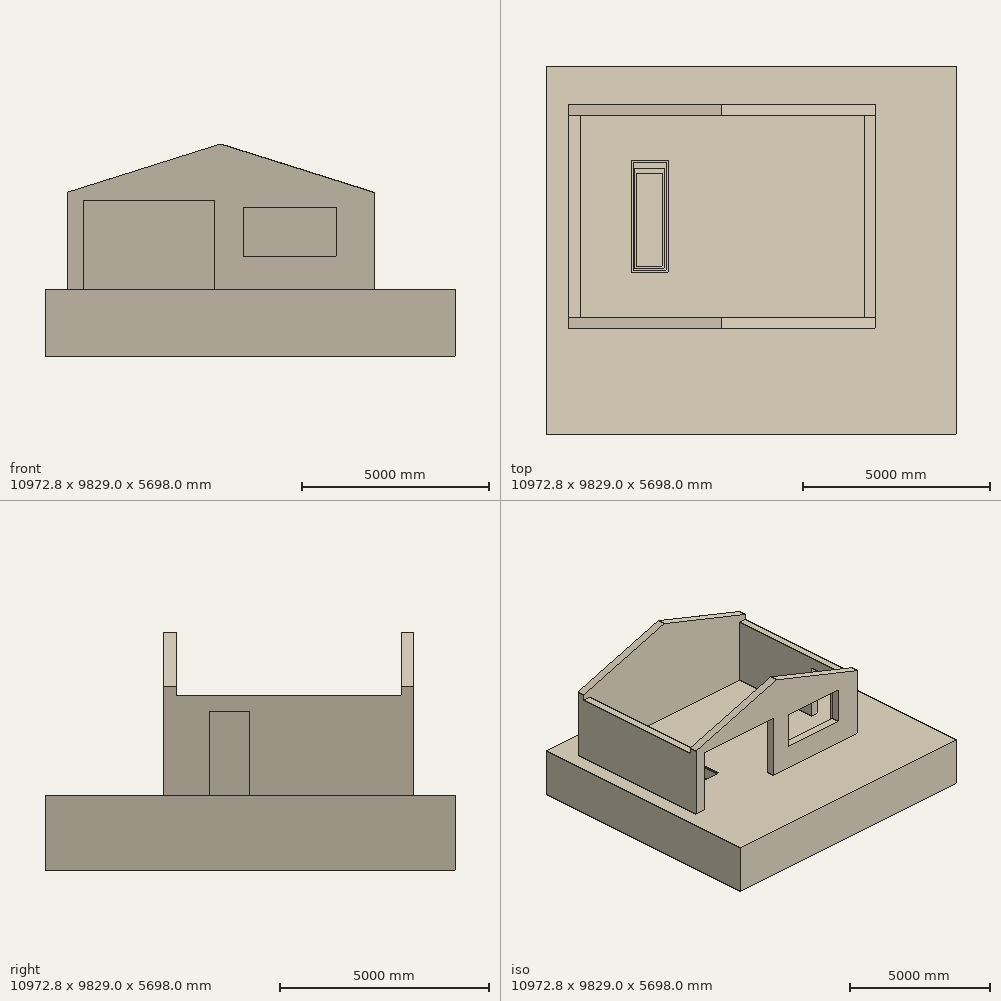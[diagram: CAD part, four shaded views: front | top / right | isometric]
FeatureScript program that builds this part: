
annotation { "Feature Type Name" : "Feature", "Feature Type Description" : "" }
export const myFeature = defineFeature(function(context is Context, id is Id, definition is map)
    precondition{}
    {
        {
            var Q0;
            Q0=qCreatedBy(makeId("Top.planeOp"),FACE);
            var sketch = newSketch(context, id + "F0", { "sketchPlane" : qUnion([Q0])});
            skLineSegment(sketch, "E0.bottom", {"start": v(-4093.64, 2707.76) * mm, "end": v(4106.36, 2707.76) * mm});
            skLineSegment(sketch, "E0.top", {"start": v(-4093.64, -3292.24) * mm, "end": v(4106.36, -3292.24) * mm});
            skLineSegment(sketch, "E0.left", {"start": v(-4093.64, 2707.76) * mm, "end": v(-4093.64, -3292.24) * mm});
            skLineSegment(sketch, "E0.right", {"start": v(4106.36, 2707.76) * mm, "end": v(4106.36, -3292.24) * mm});
            skSolve(sketch);
        }
        {
            var Q0;
            Q0=makeQuery(id+"F0.imprint","IMPRINT",FACE,{"disambiguationData":[TD([[makeQuery(id+"F0.imprint","IMPRINT",EDGE,{"derivedFrom":sQuery(id+"F0.wireOp",EDGE,"E0.bottom")}),-1.0]])]});
            extrude(context, id + "F1", {"entities" : qUnion([Q0]), "depth" : 2400 * mm, "offsetDistance" : 25 * mm});
        }
        {
            var Q0;
            Q0=makeQuery(id+"F1.opExtrude","CAP_FACE",FACE,{"disambiguationData":[OSD([sQuery(id+"F0.wireOp",EDGE,"E0.bottom"),sQuery(id+"F0.wireOp",EDGE,"E0.top"),sQuery(id+"F0.wireOp",EDGE,"E0.left"),sQuery(id+"F0.wireOp",EDGE,"E0.right")])],"isStart":false});
            var sketch = newSketch(context, id + "F2", { "sketchPlane" : qUnion([Q0])});
            skLineSegment(sketch, "E1.bottom", {"start": v(-3793.64, 2407.76) * mm, "end": v(3806.36, 2407.76) * mm});
            skLineSegment(sketch, "E1.top", {"start": v(-3793.64, -2992.24) * mm, "end": v(3806.36, -2992.24) * mm});
            skLineSegment(sketch, "E1.left", {"start": v(-3793.64, 2407.76) * mm, "end": v(-3793.64, -2992.24) * mm});
            skLineSegment(sketch, "E1.right", {"start": v(3806.36, 2407.76) * mm, "end": v(3806.36, -2992.24) * mm});
            skSolve(sketch);
        }
        {
            var Q0;
            Q0 = qSketchRegion(id + "F2", true);
            extrude(context, id + "F3", {"entities" : qUnion([Q0]), "operationType" : NewBodyOperationType.REMOVE, "endBound" : BoundingType.UP_TO_NEXT, "oppositeDirection" : true, "depth" : 25 * mm, "offsetDistance" : 25 * mm});
        }
        {
            var Q0;
            Q0=makeQuery(id+"F1.opExtrude","CAP_FACE",FACE,{"disambiguationData":[OSD([sQuery(id+"F0.wireOp",EDGE,"E0.bottom"),sQuery(id+"F0.wireOp",EDGE,"E0.top"),sQuery(id+"F0.wireOp",EDGE,"E0.left"),sQuery(id+"F0.wireOp",EDGE,"E0.right")])],"isStart":true});
            var sketch = newSketch(context, id + "F4", { "sketchPlane" : qUnion([Q0])});
            skLineSegment(sketch, "E2.bottom", {"start": v(-4693.64, -3707.76) * mm, "end": v(6279.16, -3707.76) * mm});
            skLineSegment(sketch, "E2.top", {"start": v(-4693.64, 6121.2) * mm, "end": v(6279.16, 6121.2) * mm});
            skLineSegment(sketch, "E2.left", {"start": v(-4693.64, -3707.76) * mm, "end": v(-4693.64, 6121.2) * mm});
            skLineSegment(sketch, "E2.right", {"start": v(6279.16, -3707.76) * mm, "end": v(6279.16, 6121.2) * mm});
            skSolve(sketch);
        }
        {
            var Q0;
            Q0 = qSketchRegion(id + "F4", true);
            extrude(context, id + "F5", {"entities" : qUnion([Q0]), "operationType" : NewBodyOperationType.ADD, "depth" : 1800 * mm, "offsetDistance" : 25 * mm});
        }
        {
            var Q0;
            Q0=makeQuery(id+"F1.opExtrude","SWEPT_FACE",FACE,{"disambiguationData":[OSD([sQuery(id+"F0.wireOp",EDGE,"E0.top")])]});
            var sketch = newSketch(context, id + "F6", { "sketchPlane" : qUnion([Q0])});
            skLineSegment(sketch, "E3.bottom", {"start": v(-3678.64, 2375) * mm, "end": v(-178.64, 2375) * mm});
            skLineSegment(sketch, "E3.top", {"start": v(-3678.64, 0) * mm, "end": v(-178.64, 0) * mm});
            skLineSegment(sketch, "E3.left", {"start": v(-3678.64, 2375) * mm, "end": v(-3678.64, 0) * mm});
            skLineSegment(sketch, "E3.right", {"start": v(-178.64, 2375) * mm, "end": v(-178.64, 0) * mm});
            skSolve(sketch);
        }
        {
            var Q0;
            Q0 = qSketchRegion(id + "F6", true);
            extrude(context, id + "F7", {"entities" : qUnion([Q0]), "operationType" : NewBodyOperationType.REMOVE, "endBound" : BoundingType.UP_TO_NEXT, "oppositeDirection" : true, "depth" : 25 * mm, "offsetDistance" : 25 * mm});
        }
        {
            var Q0;
            Q0=makeQuery(id+"F1.opExtrude","SWEPT_FACE",FACE,{"disambiguationData":[OSD([sQuery(id+"F0.wireOp",EDGE,"E0.top")])]});
            var sketch = newSketch(context, id + "F8", { "sketchPlane" : qUnion([Q0])});
            skLineSegment(sketch, "E4.bottom", {"start": v(606.36, 2208.56) * mm, "end": v(3106.36, 2208.56) * mm});
            skLineSegment(sketch, "E4.top", {"start": v(606.36, 900) * mm, "end": v(3106.36, 900) * mm});
            skLineSegment(sketch, "E4.left", {"start": v(606.36, 2208.56) * mm, "end": v(606.36, 900) * mm});
            skLineSegment(sketch, "E4.right", {"start": v(3106.36, 2208.56) * mm, "end": v(3106.36, 900) * mm});
            skSolve(sketch);
        }
        {
            var Q0;
            {var subQ10=sQuery(id+"F8.wireOp",EDGE,"E4.top");Q0=makeQuery(id+"F8.imprint","IMPRINT",FACE,{"disambiguationData":[TD([[makeQuery(id+"F8.imprint","IMPRINT",EDGE,{"derivedFrom":subQ10}),-1.0]])]});}
            var sketch = newSketch(context, id + "F9", { "sketchPlane" : qUnion([Q0])});
            skLineSegment(sketch, "E5", {"start": v(-4093.64, 2607.28) * mm, "end": v(0, 3898) * mm});
            skLineSegment(sketch, "E6", {"start": v(0, 3898) * mm, "end": v(4106.36, 2603.27) * mm});
            skLineSegment(sketch, "E7", {"start": v(-4093.64, 2400) * mm, "end": v(-4093.64, 2607.28) * mm});
            skLineSegment(sketch, "E8", {"start": v(4106.36, 2400) * mm, "end": v(4106.36, 2603.27) * mm});
            skLineSegment(sketch, "E9", {"start": v(-4093.64, 2400) * mm, "end": v(4106.36, 2400) * mm});
            skSolve(sketch);
        }
        {
            var Q0;
            Q0 = qSketchRegion(id + "F9", true);
            extrude(context, id + "F10", {"entities" : qUnion([Q0]), "operationType" : NewBodyOperationType.ADD, "oppositeDirection" : true, "depth" : 300 * mm, "offsetDistance" : 25 * mm});
        }
        {
            var Q0;
            Q0 = qSketchRegion(id + "F8", true);
            extrude(context, id + "F11", {"entities" : qUnion([Q0]), "operationType" : NewBodyOperationType.REMOVE, "endBound" : BoundingType.UP_TO_NEXT, "oppositeDirection" : true, "depth" : 25 * mm, "offsetDistance" : 25 * mm});
        }
        {
            var Q0;
            Q0=makeQuery(id+"F3.boolean.opBoolean","COPY",FACE,{"derivedFrom":makeQuery(id+"F3.opExtrude","SWEPT_FACE",FACE,{"disambiguationData":[OSD([sQuery(id+"F2.wireOp",EDGE,"E1.right")])]})});
            var sketch = newSketch(context, id + "F12", { "sketchPlane" : qUnion([Q0])});
            skLineSegment(sketch, "E10.bottom", {"start": v(1242.24, 2000) * mm, "end": v(2192.24, 2000) * mm});
            skLineSegment(sketch, "E10.top", {"start": v(1242.24, 0) * mm, "end": v(2192.24, 0) * mm});
            skLineSegment(sketch, "E10.left", {"start": v(1242.24, 2000) * mm, "end": v(1242.24, 0) * mm});
            skLineSegment(sketch, "E10.right", {"start": v(2192.24, 2000) * mm, "end": v(2192.24, 0) * mm});
            skSolve(sketch);
        }
        {
            var Q0;
            Q0 = qSketchRegion(id + "F12", true);
            extrude(context, id + "F13", {"entities" : qUnion([Q0]), "operationType" : NewBodyOperationType.REMOVE, "endBound" : BoundingType.UP_TO_NEXT, "oppositeDirection" : true, "depth" : 25 * mm, "offsetDistance" : 25 * mm});
        }
        {
            var Q0;
            Q0=makeQuery(id+"F1.opExtrude","SWEPT_FACE",FACE,{"disambiguationData":[OSD([sQuery(id+"F0.wireOp",EDGE,"E0.bottom")])]});
            var sketch = newSketch(context, id + "F14", { "sketchPlane" : qUnion([Q0])});
            skLineSegment(sketch, "E11", {"start": v(-4106.36, 2400) * mm, "end": v(-4106.36, 2603.27) * mm});
            skLineSegment(sketch, "E12", {"start": v(-4106.36, 2603.27) * mm, "end": v(0, 3898) * mm});
            skLineSegment(sketch, "E13", {"start": v(0, 3898) * mm, "end": v(4093.64, 2607.28) * mm});
            skLineSegment(sketch, "E14", {"start": v(4093.64, 2607.28) * mm, "end": v(4093.64, 2400) * mm});
            skLineSegment(sketch, "E15", {"start": v(-4106.36, 2400) * mm, "end": v(4093.64, 2400) * mm});
            skSolve(sketch);
        }
        {
            var Q0;
            Q0 = qSketchRegion(id + "F14", true);
            extrude(context, id + "F15", {"entities" : qUnion([Q0]), "operationType" : NewBodyOperationType.ADD, "oppositeDirection" : true, "depth" : 300 * mm, "offsetDistance" : 25 * mm});
        }
        {
            var Q0;
            {var subQ0=sQuery(id+"F4.wireOp",EDGE,"E2.right");var subQ1=sQuery(id+"F4.wireOp",EDGE,"E2.left");var subQ2=sQuery(id+"F4.wireOp",EDGE,"E2.top");var subQ3=sQuery(id+"F4.wireOp",EDGE,"E2.bottom");var subQ4=makeQuery(id+"F5.opExtrude","CAP_FACE",FACE,{"disambiguationData":[OSD([subQ3,subQ2,subQ1,subQ0])],"isStart":true});Q0=makeQuery(id+"F13.boolean.opBoolean","MERGE",FACE,{"derivedFrom":[makeQuery(id+"F7.boolean.opBoolean","MERGE",FACE,{"derivedFrom":[makeQuery(id+"F5.boolean.opBoolean","SPLIT",FACE,{"disambiguationData":[TD([makeQuery(id+"F1.opExtrude","SWEPT_FACE",FACE,{"disambiguationData":[OSD([sQuery(id+"F0.wireOp",EDGE,"E0.bottom")])]})])],"derivedFrom":subQ4}),makeQuery(id+"F5.boolean.opBoolean","SPLIT",FACE,{"disambiguationData":[TD([makeQuery(id+"F3.boolean.opBoolean","COPY",FACE,{"derivedFrom":makeQuery(id+"F3.opExtrude","SWEPT_FACE",FACE,{"disambiguationData":[OSD([sQuery(id+"F2.wireOp",EDGE,"E1.bottom")])]})})])],"derivedFrom":subQ4}),makeQuery(id+"F7.opExtrude","SWEPT_FACE",FACE,{"disambiguationData":[OSD([sQuery(id+"F6.wireOp",EDGE,"E3.top")])]})]}),makeQuery(id+"F13.opExtrude","SWEPT_FACE",FACE,{"disambiguationData":[OSD([sQuery(id+"F12.wireOp",EDGE,"E10.top")])]})]});}
            var sketch = newSketch(context, id + "F16", { "sketchPlane" : qUnion([Q0])});
            skLineSegment(sketch, "E16.bottom", {"start": v(-2428.64, 1207.76) * mm, "end": v(-1428.64, 1207.76) * mm});
            skLineSegment(sketch, "E16.top", {"start": v(-2428.64, -1792.24) * mm, "end": v(-1428.64, -1792.24) * mm});
            skLineSegment(sketch, "E16.left", {"start": v(-2428.64, 1207.76) * mm, "end": v(-2428.64, -1792.24) * mm});
            skLineSegment(sketch, "E16.right", {"start": v(-1428.64, 1207.76) * mm, "end": v(-1428.64, -1792.24) * mm});
            skLineSegment(sketch, "E17", {"start": v(-3678.64, -3292.24) * mm, "end": v(-178.64, -3292.24) * mm});
            skLineSegment(sketch, "E18", {"start": v(-178.64, -3292.24) * mm, "end": v(-1928.64, -3292.24) * mm});
            skLineSegment(sketch, "E19", {"start": v(-1928.64, 1207.76) * mm, "end": v(-1928.64, -1792.24) * mm, "construction": true});
            skLineSegment(sketch, "E20", {"start": v(-1928.64, -3292.24) * mm, "end": v(-1928.64, 2407.76) * mm, "construction": true});
            skPoint(sketch, "E21.startSnap0", {"position": v(-1928.64, -442.24) * mm});
            skLineSegment(sketch, "E22", {"start": v(-3793.64, -292.24) * mm, "end": v(1314.81, -292.24) * mm, "construction": true});
            skLineSegment(sketch, "E23", {"start": v(-2428.64, -292.24) * mm, "end": v(-1428.64, -292.24) * mm, "construction": true});
            skSolve(sketch);
        }
        {
            var Q0;
            Q0 = qSketchRegion(id + "F16", true);
            extrude(context, id + "F17", {"entities" : qUnion([Q0]), "operationType" : NewBodyOperationType.REMOVE, "oppositeDirection" : true, "depth" : 30 * mm, "offsetDistance" : 25 * mm});
        }
        {
            var Q0;
            Q0=makeQuery(id+"F17.boolean.opBoolean","COPY",FACE,{"derivedFrom":makeQuery(id+"F17.opExtrude","CAP_FACE",FACE,{"disambiguationData":[OSD([sQuery(id+"F16.wireOp",EDGE,"E16.bottom"),sQuery(id+"F16.wireOp",EDGE,"E16.top"),sQuery(id+"F16.wireOp",EDGE,"E16.left"),sQuery(id+"F16.wireOp",EDGE,"E16.right")])],"isStart":false})});
            var sketch = newSketch(context, id + "F18", { "sketchPlane" : qUnion([Q0])});
            skLineSegment(sketch, "E24.bottom", {"start": v(-2378.64, 1157.76) * mm, "end": v(-1478.64, 1157.76) * mm});
            skLineSegment(sketch, "E24.top", {"start": v(-2378.64, -1742.24) * mm, "end": v(-1478.64, -1742.24) * mm});
            skLineSegment(sketch, "E24.left", {"start": v(-2378.64, 1157.76) * mm, "end": v(-2378.64, -1742.24) * mm});
            skLineSegment(sketch, "E24.right", {"start": v(-1478.64, 1157.76) * mm, "end": v(-1478.64, -1742.24) * mm});
            skSolve(sketch);
        }
        {
            var Q0;
            Q0 = qSketchRegion(id + "F18", true);
            extrude(context, id + "F19", {"entities" : qUnion([Q0]), "operationType" : NewBodyOperationType.REMOVE, "oppositeDirection" : true, "depth" : 423.33 * mm, "offsetDistance" : 25 * mm});
        }
        {
            var Q0;
            Q0=makeQuery(id+"F19.boolean.opBoolean","COPY",FACE,{"derivedFrom":makeQuery(id+"F19.opExtrude","CAP_FACE",FACE,{"disambiguationData":[OSD([sQuery(id+"F18.wireOp",EDGE,"E24.bottom"),sQuery(id+"F18.wireOp",EDGE,"E24.top"),sQuery(id+"F18.wireOp",EDGE,"E24.left"),sQuery(id+"F18.wireOp",EDGE,"E24.right")])],"isStart":false})});
            var sketch = newSketch(context, id + "F20", { "sketchPlane" : qUnion([Q0])});
            skLineSegment(sketch, "E25.bottom", {"start": v(-2328.64, 982.76) * mm, "end": v(-1528.64, 982.76) * mm});
            skLineSegment(sketch, "E25.top", {"start": v(-2328.64, -1692.24) * mm, "end": v(-1528.64, -1692.24) * mm});
            skLineSegment(sketch, "E25.left", {"start": v(-2328.64, 982.76) * mm, "end": v(-2328.64, -1692.24) * mm});
            skLineSegment(sketch, "E25.right", {"start": v(-1528.64, 982.76) * mm, "end": v(-1528.64, -1692.24) * mm});
            skSolve(sketch);
        }
        {
            var Q0;
            Q0 = qSketchRegion(id + "F20", true);
            extrude(context, id + "F21", {"entities" : qUnion([Q0]), "operationType" : NewBodyOperationType.REMOVE, "oppositeDirection" : true, "depth" : 423.33 * mm, "offsetDistance" : 25 * mm});
        }
        {
            var Q0;
            Q0=makeQuery(id+"F21.boolean.opBoolean","COPY",FACE,{"derivedFrom":makeQuery(id+"F21.opExtrude","CAP_FACE",FACE,{"disambiguationData":[OSD([sQuery(id+"F20.wireOp",EDGE,"E25.bottom"),sQuery(id+"F20.wireOp",EDGE,"E25.top"),sQuery(id+"F20.wireOp",EDGE,"E25.left"),sQuery(id+"F20.wireOp",EDGE,"E25.right")])],"isStart":false})});
            var sketch = newSketch(context, id + "F22", { "sketchPlane" : qUnion([Q0])});
            skLineSegment(sketch, "E26.bottom", {"start": v(-2278.64, 857.76) * mm, "end": v(-1578.64, 857.76) * mm});
            skLineSegment(sketch, "E26.top", {"start": v(-2278.64, -1642.24) * mm, "end": v(-1578.64, -1642.24) * mm});
            skLineSegment(sketch, "E26.left", {"start": v(-2278.64, 857.76) * mm, "end": v(-2278.64, -1642.24) * mm});
            skLineSegment(sketch, "E26.right", {"start": v(-1578.64, 857.76) * mm, "end": v(-1578.64, -1642.24) * mm});
            skSolve(sketch);
        }
        {
            var Q0;
            Q0 = qSketchRegion(id + "F22", true);
            extrude(context, id + "F23", {"entities" : qUnion([Q0]), "operationType" : NewBodyOperationType.REMOVE, "oppositeDirection" : true, "depth" : 423.33 * mm, "offsetDistance" : 25 * mm});
        }
    });
